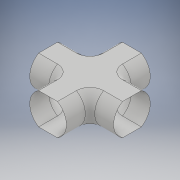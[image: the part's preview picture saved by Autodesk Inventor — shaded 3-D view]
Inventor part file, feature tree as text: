
AUTODESK INVENTOR PART (.ipt)
format: ipt  version: 2017 (Build 210142000, 142)  size: 222,208 bytes
history: native  units: in
note: dims shown in document units (in); Inventor stores cm internally (conversion verified against a paired STEP export)
features: sketch x4, extrude x3, mirror x3, plane x1, sweep x1, delete_face x1, other x1
ambient origin geometry x8: Origin, YZ Plane, XZ Plane, XY Plane, X Axis, Y Axis, Z Axis, Center Point
bodies: Body1 (feature_tree)
feature tree (14):
  extrude  "corridor eighth"  Depth=9.7746in TaperAngle=45.0deg
  plane  "Work Plane1"
  sketch  "Sketch17"  dims[d160=4.0in d168=10.3167in d169=10.3167in]
  sketch  "Sketch7"  dims[d0=6.6667in d2=9.7746in d5=-4.8873in d62=45.0deg d71=4.0in d72=0.0in]
  sweep  "curve"
  mirror  "mirror plane YZ"
  extrude  "corridor eighth complete"  Depth=10.3167in
  mirror  "Mirror half"
  mirror  "Mirrorfull"
  extrude  "hole fill in"  Depth=3.3333in
  delete_face  "Delete Face1"
  other  "corridor"
  sketch  "Sketch22"  dims[d170=10.3167in d171=10.3167in]
  sketch  "Sketch24"  dims[d196=4.0in d198=3.8873in d199=3.8873in d203=1.6458in d209=3.3333in d211=1.0in d212=0.0in d213=0.0in d214=4.0in d215=0.0in d216=4.0in d217=0.0in]
